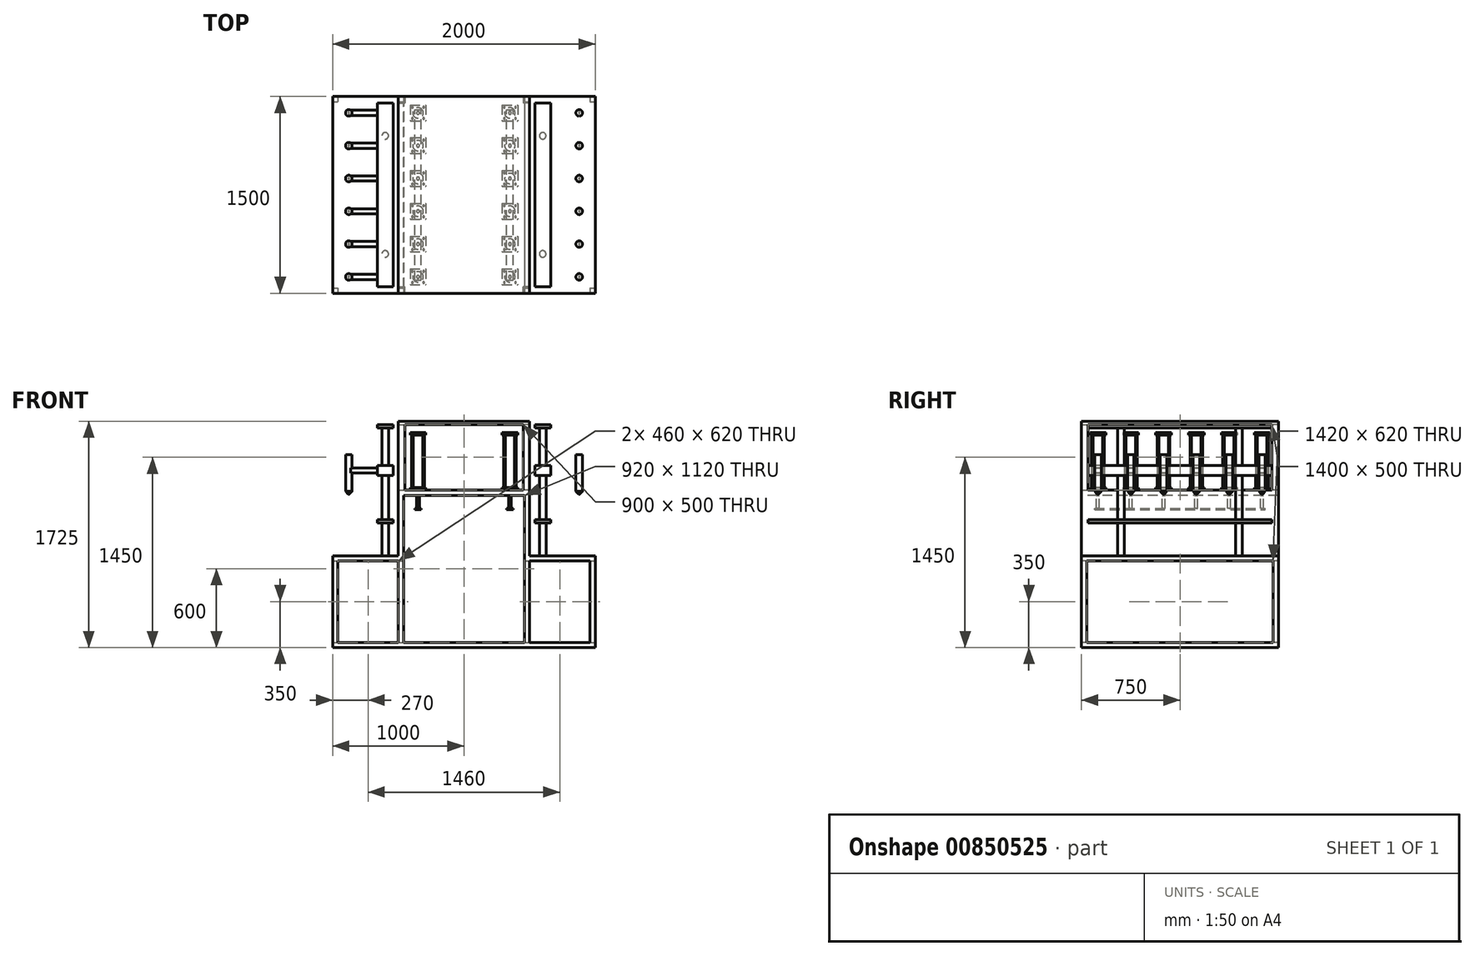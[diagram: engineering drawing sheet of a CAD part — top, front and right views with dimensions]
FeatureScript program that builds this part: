
annotation { "Feature Type Name" : "Feature", "Feature Type Description" : "" }
export const myFeature = defineFeature(function(context is Context, id is Id, definition is map)
    precondition{}
    {
        {
            var Q0;
            Q0=qCreatedBy(makeId("Front.planeOp"),FACE);
            var sketch = newSketch(context, id + "F0", { "sketchPlane" : qUnion([Q0])});
            skLineSegment(sketch, "E0", {"start": v(0, 0) * mm, "end": v(1000, 0) * mm});
            skLineSegment(sketch, "E1", {"start": v(1000, 0) * mm, "end": v(1000, 700) * mm});
            skLineSegment(sketch, "E2", {"start": v(1000, 700) * mm, "end": v(500, 700) * mm});
            skLineSegment(sketch, "E3", {"start": v(500, 700) * mm, "end": v(500, 1200) * mm});
            skLineSegment(sketch, "E4", {"start": v(500, 1200) * mm, "end": v(0, 1200) * mm});
            skLineSegment(sketch, "E5", {"start": v(0, 1200) * mm, "end": v(0, 0) * mm});
            skLineSegment(sketch, "E6.MirrorCS", {"start": v(-500, 1200) * mm, "end": v(0, 1200) * mm});
            skLineSegment(sketch, "E7.MirrorCS", {"start": v(-500, 700) * mm, "end": v(-500, 1200) * mm});
            skLineSegment(sketch, "E8.MirrorCS", {"start": v(-1000, 700) * mm, "end": v(-500, 700) * mm});
            skLineSegment(sketch, "E9.MirrorCS", {"start": v(-1000, 0) * mm, "end": v(-1000, 700) * mm});
            skLineSegment(sketch, "E10.MirrorCS", {"start": v(0, 0) * mm, "end": v(-1000, 0) * mm});
            skSolve(sketch);
        }
        {
            var Q0;
            Q0=makeQuery(id+"F0.imprint","IMPRINT",FACE,{"disambiguationData":[TD([[makeQuery(id+"F0.imprint","IMPRINT",EDGE,{"derivedFrom":sQuery(id+"F0.wireOp",EDGE,"E5")}),-1.0]])]});
            var Q1;
            Q1=makeQuery(id+"F0.imprint","IMPRINT",FACE,{"disambiguationData":[TD([[makeQuery(id+"F0.imprint","IMPRINT",EDGE,{"derivedFrom":sQuery(id+"F0.wireOp",EDGE,"E0")}),1.0]])]});
            extrude(context, id + "F1", {"entities" : qUnion([Q0, Q1]), "depth" : 1500 * mm, "offsetDistance" : 25 * mm});
        }
        {
            var Q0;
            Q0=makeQuery(id+"F1.opExtrude","CAP_FACE",FACE,{"disambiguationData":[OSD([sQuery(id+"F0.wireOp",EDGE,"E0"),sQuery(id+"F0.wireOp",EDGE,"E1"),sQuery(id+"F0.wireOp",EDGE,"E2"),sQuery(id+"F0.wireOp",EDGE,"E3"),sQuery(id+"F0.wireOp",EDGE,"E4"),sQuery(id+"F0.wireOp",EDGE,"E6.MirrorCS"),sQuery(id+"F0.wireOp",EDGE,"E7.MirrorCS"),sQuery(id+"F0.wireOp",EDGE,"E8.MirrorCS"),sQuery(id+"F0.wireOp",EDGE,"E9.MirrorCS"),sQuery(id+"F0.wireOp",EDGE,"E10.MirrorCS")])],"isStart":false});
            var sketch = newSketch(context, id + "F2", { "sketchPlane" : qUnion([Q0])});
            skLineSegment(sketch, "E11.0", {"start": v(-960, 660) * mm, "end": v(-960, 40) * mm});
            skLineSegment(sketch, "E11.1", {"start": v(-500, 660) * mm, "end": v(-960, 660) * mm});
            skLineSegment(sketch, "E11.2", {"start": v(-960, 40) * mm, "end": v(-500, 40) * mm});
            skLineSegment(sketch, "E11.3", {"start": v(-460, 1160) * mm, "end": v(-460, 660) * mm});
            skLineSegment(sketch, "E11.4", {"start": v(960, 40) * mm, "end": v(960, 660) * mm});
            skLineSegment(sketch, "E11.5", {"start": v(960, 660) * mm, "end": v(500, 660) * mm});
            skLineSegment(sketch, "E11.6", {"start": v(460, 660) * mm, "end": v(460, 1160) * mm});
            skLineSegment(sketch, "E11.7", {"start": v(460, 1160) * mm, "end": v(-460, 1160) * mm});
            skLineSegment(sketch, "E12", {"start": v(-460, 660) * mm, "end": v(-460, 40) * mm});
            skLineSegment(sketch, "E13.0", {"start": v(-500, 660) * mm, "end": v(-500, 40) * mm});
            skLineSegment(sketch, "E14.trimOffspring", {"start": v(-460, 40) * mm, "end": v(460, 40) * mm});
            skLineSegment(sketch, "E15", {"start": v(460, 660) * mm, "end": v(460, 40) * mm});
            skLineSegment(sketch, "E16.0", {"start": v(500, 660) * mm, "end": v(500, 40) * mm});
            skLineSegment(sketch, "E17.trimOffspring", {"start": v(500, 40) * mm, "end": v(960, 40) * mm});
            skSolve(sketch);
        }
        {
            var Q0;
            Q0=makeQuery(id+"F2.imprint","IMPRINT",FACE,{"disambiguationData":[TD([[makeQuery(id+"F2.imprint","IMPRINT",EDGE,{"derivedFrom":sQuery(id+"F2.wireOp",EDGE,"E11.0")}),1.0]])]});
            var Q1;
            Q1=makeQuery(id+"F2.imprint","IMPRINT",FACE,{"disambiguationData":[TD([[makeQuery(id+"F2.imprint","IMPRINT",EDGE,{"derivedFrom":sQuery(id+"F2.wireOp",EDGE,"E11.4")}),1.0]])]});
            var Q2;
            Q2=makeQuery(id+"F2.imprint","IMPRINT",FACE,{"disambiguationData":[TD([[makeQuery(id+"F2.imprint","IMPRINT",EDGE,{"derivedFrom":sQuery(id+"F2.wireOp",EDGE,"E11.3")}),1.0]])]});
            extrude(context, id + "F3", {"entities" : qUnion([Q0, Q1, Q2]), "operationType" : NewBodyOperationType.REMOVE, "endBound" : BoundingType.THROUGH_ALL, "oppositeDirection" : true, "depth" : 25 * mm, "offsetDistance" : 25 * mm});
        }
        {
            var Q0;
            Q0=makeQuery(id+"F1.opExtrude","SWEPT_FACE",FACE,{"disambiguationData":[OSD([sQuery(id+"F0.wireOp",EDGE,"E1")])]});
            var sketch = newSketch(context, id + "F4", { "sketchPlane" : qUnion([Q0])});
            skLineSegment(sketch, "E18.0", {"start": v(-40, 40) * mm, "end": v(-40, 660) * mm});
            skLineSegment(sketch, "E18.1", {"start": v(-1460, 40) * mm, "end": v(-40, 40) * mm});
            skLineSegment(sketch, "E18.2", {"start": v(-1460, 660) * mm, "end": v(-1460, 40) * mm});
            skLineSegment(sketch, "E18.3", {"start": v(-40, 660) * mm, "end": v(-1460, 660) * mm});
            skSolve(sketch);
        }
        {
            var Q0;
            Q0=makeQuery(id+"F4.imprint","IMPRINT",FACE,{"disambiguationData":[TD([[makeQuery(id+"F4.imprint","IMPRINT",EDGE,{"derivedFrom":sQuery(id+"F4.wireOp",EDGE,"E18.0")}),1.0]])]});
            extrude(context, id + "F5", {"entities" : qUnion([Q0]), "operationType" : NewBodyOperationType.REMOVE, "endBound" : BoundingType.THROUGH_ALL, "oppositeDirection" : true, "depth" : 25 * mm, "offsetDistance" : 25 * mm});
        }
        {
            var Q0;
            Q0=makeQuery(id+"F1.opExtrude","SWEPT_FACE",FACE,{"disambiguationData":[OSD([sQuery(id+"F0.wireOp",EDGE,"E4"),sQuery(id+"F0.wireOp",EDGE,"E6.MirrorCS")])]});
            var sketch = newSketch(context, id + "F6", { "sketchPlane" : qUnion([Q0])});
            skLineSegment(sketch, "E19.bottom", {"start": v(-410, -65) * mm, "end": v(-290, -65) * mm});
            skLineSegment(sketch, "E19.top", {"start": v(-410, -185) * mm, "end": v(-290, -185) * mm});
            skLineSegment(sketch, "E19.left", {"start": v(-410, -65) * mm, "end": v(-410, -185) * mm});
            skLineSegment(sketch, "E19.right", {"start": v(-290, -65) * mm, "end": v(-290, -185) * mm});
            skLineSegment(sketch, "E20.0.1.0", {"start": v(-410, -315) * mm, "end": v(-410, -435) * mm});
            skLineSegment(sketch, "E20.0.1.1", {"start": v(-290, -315) * mm, "end": v(-290, -435) * mm});
            skLineSegment(sketch, "E20.0.1.2", {"start": v(-410, -435) * mm, "end": v(-290, -435) * mm});
            skLineSegment(sketch, "E20.0.1.3", {"start": v(-410, -315) * mm, "end": v(-290, -315) * mm});
            skLineSegment(sketch, "E20.0.2.0", {"start": v(-410, -565) * mm, "end": v(-410, -685) * mm});
            skLineSegment(sketch, "E20.0.2.1", {"start": v(-290, -565) * mm, "end": v(-290, -685) * mm});
            skLineSegment(sketch, "E20.0.2.2", {"start": v(-410, -685) * mm, "end": v(-290, -685) * mm});
            skLineSegment(sketch, "E20.0.2.3", {"start": v(-410, -565) * mm, "end": v(-290, -565) * mm});
            skLineSegment(sketch, "E20.0.3.0", {"start": v(-410, -815) * mm, "end": v(-410, -935) * mm});
            skLineSegment(sketch, "E20.0.3.1", {"start": v(-290, -815) * mm, "end": v(-290, -935) * mm});
            skLineSegment(sketch, "E20.0.3.2", {"start": v(-410, -935) * mm, "end": v(-290, -935) * mm});
            skLineSegment(sketch, "E20.0.3.3", {"start": v(-410, -815) * mm, "end": v(-290, -815) * mm});
            skLineSegment(sketch, "E20.0.4.0", {"start": v(-410, -1065) * mm, "end": v(-410, -1185) * mm});
            skLineSegment(sketch, "E20.0.4.1", {"start": v(-290, -1065) * mm, "end": v(-290, -1185) * mm});
            skLineSegment(sketch, "E20.0.4.2", {"start": v(-410, -1185) * mm, "end": v(-290, -1185) * mm});
            skLineSegment(sketch, "E20.0.4.3", {"start": v(-410, -1065) * mm, "end": v(-290, -1065) * mm});
            skLineSegment(sketch, "E20.0.5.0", {"start": v(-410, -1315) * mm, "end": v(-410, -1435) * mm});
            skLineSegment(sketch, "E20.0.5.1", {"start": v(-290, -1315) * mm, "end": v(-290, -1435) * mm});
            skLineSegment(sketch, "E20.0.5.2", {"start": v(-410, -1435) * mm, "end": v(-290, -1435) * mm});
            skLineSegment(sketch, "E20.0.5.3", {"start": v(-410, -1315) * mm, "end": v(-290, -1315) * mm});
            skLineSegment(sketch, "E20.1.0.0", {"start": v(290, -65) * mm, "end": v(290, -185) * mm});
            skLineSegment(sketch, "E20.1.0.1", {"start": v(410, -65) * mm, "end": v(410, -185) * mm});
            skLineSegment(sketch, "E20.1.0.2", {"start": v(290, -185) * mm, "end": v(410, -185) * mm});
            skLineSegment(sketch, "E20.1.0.3", {"start": v(290, -65) * mm, "end": v(410, -65) * mm});
            skLineSegment(sketch, "E20.1.1.0", {"start": v(290, -315) * mm, "end": v(290, -435) * mm});
            skLineSegment(sketch, "E20.1.1.1", {"start": v(410, -315) * mm, "end": v(410, -435) * mm});
            skLineSegment(sketch, "E20.1.1.2", {"start": v(290, -435) * mm, "end": v(410, -435) * mm});
            skLineSegment(sketch, "E20.1.1.3", {"start": v(290, -315) * mm, "end": v(410, -315) * mm});
            skLineSegment(sketch, "E20.1.2.0", {"start": v(290, -565) * mm, "end": v(290, -685) * mm});
            skLineSegment(sketch, "E20.1.2.1", {"start": v(410, -565) * mm, "end": v(410, -685) * mm});
            skLineSegment(sketch, "E20.1.2.2", {"start": v(290, -685) * mm, "end": v(410, -685) * mm});
            skLineSegment(sketch, "E20.1.2.3", {"start": v(290, -565) * mm, "end": v(410, -565) * mm});
            skLineSegment(sketch, "E20.1.3.0", {"start": v(290, -815) * mm, "end": v(290, -935) * mm});
            skLineSegment(sketch, "E20.1.3.1", {"start": v(410, -815) * mm, "end": v(410, -935) * mm});
            skLineSegment(sketch, "E20.1.3.2", {"start": v(290, -935) * mm, "end": v(410, -935) * mm});
            skLineSegment(sketch, "E20.1.3.3", {"start": v(290, -815) * mm, "end": v(410, -815) * mm});
            skLineSegment(sketch, "E20.1.4.0", {"start": v(290, -1065) * mm, "end": v(290, -1185) * mm});
            skLineSegment(sketch, "E20.1.4.1", {"start": v(410, -1065) * mm, "end": v(410, -1185) * mm});
            skLineSegment(sketch, "E20.1.4.2", {"start": v(290, -1185) * mm, "end": v(410, -1185) * mm});
            skLineSegment(sketch, "E20.1.4.3", {"start": v(290, -1065) * mm, "end": v(410, -1065) * mm});
            skLineSegment(sketch, "E20.1.5.0", {"start": v(290, -1315) * mm, "end": v(290, -1435) * mm});
            skLineSegment(sketch, "E20.1.5.1", {"start": v(410, -1315) * mm, "end": v(410, -1435) * mm});
            skLineSegment(sketch, "E20.1.5.2", {"start": v(290, -1435) * mm, "end": v(410, -1435) * mm});
            skLineSegment(sketch, "E20.1.5.3", {"start": v(290, -1315) * mm, "end": v(410, -1315) * mm});
            skLineSegment(sketch, "E20.direction1", {"start": v(-410, -185) * mm, "end": v(290, -185) * mm, "construction": true});
            skLineSegment(sketch, "E20.direction2", {"start": v(-410, -185) * mm, "end": v(-410, -435) * mm, "construction": true});
            skSolve(sketch);
        }
        {
            var Q0;
            Q0 = qSketchRegion(id + "F6", true);
            extrude(context, id + "F7", {"entities" : qUnion([Q0]), "operationType" : NewBodyOperationType.ADD, "depth" : 20 * mm, "offsetDistance" : 25 * mm});
        }
        {
            var Q0;
            Q0=makeQuery(id+"F7.opExtrude","CAP_FACE",FACE,{"disambiguationData":[OSD([sQuery(id+"F6.wireOp",EDGE,"E20.0.5.0"),sQuery(id+"F6.wireOp",EDGE,"E20.0.5.1"),sQuery(id+"F6.wireOp",EDGE,"E20.0.5.2"),sQuery(id+"F6.wireOp",EDGE,"E20.0.5.3")])],"isStart":false});
            var sketch = newSketch(context, id + "F8", { "sketchPlane" : qUnion([Q0])});
            skCircle(sketch, "E21", {"center": v(-350, -1375) * mm, "radius": 40 * mm});
            skPoint(sketch, "E21.centerSnap0", {"position": v(-290, -1375) * mm});
            skPoint(sketch, "E21.centerSnap1", {"position": v(-350, -1315) * mm});
            skCircle(sketch, "E22.0.1.0", {"center": v(-350, -1125) * mm, "radius": 40 * mm});
            skCircle(sketch, "E22.0.2.0", {"center": v(-350, -875) * mm, "radius": 40 * mm});
            skCircle(sketch, "E22.0.3.0", {"center": v(-350, -625) * mm, "radius": 40 * mm});
            skCircle(sketch, "E22.0.4.0", {"center": v(-350, -375) * mm, "radius": 40 * mm});
            skCircle(sketch, "E22.0.5.0", {"center": v(-350, -125) * mm, "radius": 40 * mm});
            skCircle(sketch, "E22.1.0.0", {"center": v(350, -1375) * mm, "radius": 40 * mm});
            skCircle(sketch, "E22.1.1.0", {"center": v(350, -1125) * mm, "radius": 40 * mm});
            skCircle(sketch, "E22.1.2.0", {"center": v(350, -875) * mm, "radius": 40 * mm});
            skCircle(sketch, "E22.1.3.0", {"center": v(350, -625) * mm, "radius": 40 * mm});
            skCircle(sketch, "E22.1.4.0", {"center": v(350, -375) * mm, "radius": 40 * mm});
            skCircle(sketch, "E22.1.5.0", {"center": v(350, -125) * mm, "radius": 40 * mm});
            skLineSegment(sketch, "E22.direction1", {"start": v(-350, -1375) * mm, "end": v(350, -1375) * mm, "construction": true});
            skLineSegment(sketch, "E22.direction2", {"start": v(-350, -1375) * mm, "end": v(-350, -1125) * mm, "construction": true});
            skSolve(sketch);
        }
        {
            var Q0;
            Q0 = qSketchRegion(id + "F8", true);
            extrude(context, id + "F9", {"entities" : qUnion([Q0]), "operationType" : NewBodyOperationType.ADD, "depth" : 400 * mm, "offsetDistance" : 25 * mm});
        }
        {
            var Q0;
            Q0=makeQuery(id+"F7.opExtrude","CAP_FACE",FACE,{"disambiguationData":[OSD([sQuery(id+"F6.wireOp",EDGE,"E20.0.5.0"),sQuery(id+"F6.wireOp",EDGE,"E20.0.5.1"),sQuery(id+"F6.wireOp",EDGE,"E20.0.5.2"),sQuery(id+"F6.wireOp",EDGE,"E20.0.5.3")])],"isStart":false});
            var sketch = newSketch(context, id + "F10", { "sketchPlane" : qUnion([Q0])});
            skCircle(sketch, "E23", {"center": v(-307.5, -1332.5) * mm, "radius": 6 * mm});
            skCircle(sketch, "E24", {"center": v(-392.5, -1332.5) * mm, "radius": 6 * mm});
            skCircle(sketch, "E25", {"center": v(-307.5, -1417.5) * mm, "radius": 6 * mm});
            skCircle(sketch, "E26", {"center": v(-392.5, -1417.5) * mm, "radius": 6 * mm});
            skCircle(sketch, "E27.0.1.0", {"center": v(-307.5, -1082.5) * mm, "radius": 6 * mm});
            skCircle(sketch, "E27.0.1.1", {"center": v(-392.5, -1082.5) * mm, "radius": 6 * mm});
            skCircle(sketch, "E27.0.1.2", {"center": v(-392.5, -1167.5) * mm, "radius": 6 * mm});
            skCircle(sketch, "E27.0.1.3", {"center": v(-307.5, -1167.5) * mm, "radius": 6 * mm});
            skCircle(sketch, "E27.0.2.0", {"center": v(-307.5, -832.5) * mm, "radius": 6 * mm});
            skCircle(sketch, "E27.0.2.1", {"center": v(-392.5, -832.5) * mm, "radius": 6 * mm});
            skCircle(sketch, "E27.0.2.2", {"center": v(-392.5, -917.5) * mm, "radius": 6 * mm});
            skCircle(sketch, "E27.0.2.3", {"center": v(-307.5, -917.5) * mm, "radius": 6 * mm});
            skCircle(sketch, "E27.0.3.0", {"center": v(-307.5, -582.5) * mm, "radius": 6 * mm});
            skCircle(sketch, "E27.0.3.1", {"center": v(-392.5, -582.5) * mm, "radius": 6 * mm});
            skCircle(sketch, "E27.0.3.2", {"center": v(-392.5, -667.5) * mm, "radius": 6 * mm});
            skCircle(sketch, "E27.0.3.3", {"center": v(-307.5, -667.5) * mm, "radius": 6 * mm});
            skCircle(sketch, "E27.0.4.0", {"center": v(-307.5, -332.5) * mm, "radius": 6 * mm});
            skCircle(sketch, "E27.0.4.1", {"center": v(-392.5, -332.5) * mm, "radius": 6 * mm});
            skCircle(sketch, "E27.0.4.2", {"center": v(-392.5, -417.5) * mm, "radius": 6 * mm});
            skCircle(sketch, "E27.0.4.3", {"center": v(-307.5, -417.5) * mm, "radius": 6 * mm});
            skCircle(sketch, "E27.0.5.0", {"center": v(-307.5, -82.5) * mm, "radius": 6 * mm});
            skCircle(sketch, "E27.0.5.1", {"center": v(-392.5, -82.5) * mm, "radius": 6 * mm});
            skCircle(sketch, "E27.0.5.2", {"center": v(-392.5, -167.5) * mm, "radius": 6 * mm});
            skCircle(sketch, "E27.0.5.3", {"center": v(-307.5, -167.5) * mm, "radius": 6 * mm});
            skCircle(sketch, "E27.1.0.0", {"center": v(392.5, -1332.5) * mm, "radius": 6 * mm});
            skCircle(sketch, "E27.1.0.1", {"center": v(307.5, -1332.5) * mm, "radius": 6 * mm});
            skCircle(sketch, "E27.1.0.2", {"center": v(307.5, -1417.5) * mm, "radius": 6 * mm});
            skCircle(sketch, "E27.1.0.3", {"center": v(392.5, -1417.5) * mm, "radius": 6 * mm});
            skCircle(sketch, "E27.1.1.0", {"center": v(392.5, -1082.5) * mm, "radius": 6 * mm});
            skCircle(sketch, "E27.1.1.1", {"center": v(307.5, -1082.5) * mm, "radius": 6 * mm});
            skCircle(sketch, "E27.1.1.2", {"center": v(307.5, -1167.5) * mm, "radius": 6 * mm});
            skCircle(sketch, "E27.1.1.3", {"center": v(392.5, -1167.5) * mm, "radius": 6 * mm});
            skCircle(sketch, "E27.1.2.0", {"center": v(392.5, -832.5) * mm, "radius": 6 * mm});
            skCircle(sketch, "E27.1.2.1", {"center": v(307.5, -832.5) * mm, "radius": 6 * mm});
            skCircle(sketch, "E27.1.2.2", {"center": v(307.5, -917.5) * mm, "radius": 6 * mm});
            skCircle(sketch, "E27.1.2.3", {"center": v(392.5, -917.5) * mm, "radius": 6 * mm});
            skCircle(sketch, "E27.1.3.0", {"center": v(392.5, -582.5) * mm, "radius": 6 * mm});
            skCircle(sketch, "E27.1.3.1", {"center": v(307.5, -582.5) * mm, "radius": 6 * mm});
            skCircle(sketch, "E27.1.3.2", {"center": v(307.5, -667.5) * mm, "radius": 6 * mm});
            skCircle(sketch, "E27.1.3.3", {"center": v(392.5, -667.5) * mm, "radius": 6 * mm});
            skCircle(sketch, "E27.1.4.0", {"center": v(392.5, -332.5) * mm, "radius": 6 * mm});
            skCircle(sketch, "E27.1.4.1", {"center": v(307.5, -332.5) * mm, "radius": 6 * mm});
            skCircle(sketch, "E27.1.4.2", {"center": v(307.5, -417.5) * mm, "radius": 6 * mm});
            skCircle(sketch, "E27.1.4.3", {"center": v(392.5, -417.5) * mm, "radius": 6 * mm});
            skCircle(sketch, "E27.1.5.0", {"center": v(392.5, -82.5) * mm, "radius": 6 * mm});
            skCircle(sketch, "E27.1.5.1", {"center": v(307.5, -82.5) * mm, "radius": 6 * mm});
            skCircle(sketch, "E27.1.5.2", {"center": v(307.5, -167.5) * mm, "radius": 6 * mm});
            skCircle(sketch, "E27.1.5.3", {"center": v(392.5, -167.5) * mm, "radius": 6 * mm});
            skLineSegment(sketch, "E27.direction1", {"start": v(-392.5, -1417.5) * mm, "end": v(307.5, -1417.5) * mm, "construction": true});
            skLineSegment(sketch, "E27.direction2", {"start": v(-392.5, -1417.5) * mm, "end": v(-392.5, -1167.5) * mm, "construction": true});
            skSolve(sketch);
        }
        {
            var Q0;
            Q0 = qSketchRegion(id + "F10", true);
            extrude(context, id + "F11", {"entities" : qUnion([Q0]), "operationType" : NewBodyOperationType.ADD, "depth" : 400 * mm, "offsetDistance" : 25 * mm});
        }
        {
            var Q0;
            Q0=makeQuery(id+"F9.opExtrude","CAP_FACE",FACE,{"disambiguationData":[OSD([sQuery(id+"F8.wireOp",EDGE,"E21")])],"isStart":false});
            var sketch = newSketch(context, id + "F12", { "sketchPlane" : qUnion([Q0])});
            skLineSegment(sketch, "E28.bottom", {"start": v(-410, -1315) * mm, "end": v(-290, -1315) * mm});
            skLineSegment(sketch, "E28.top", {"start": v(-410, -1435) * mm, "end": v(-290, -1435) * mm});
            skLineSegment(sketch, "E28.left", {"start": v(-410, -1315) * mm, "end": v(-410, -1435) * mm});
            skLineSegment(sketch, "E28.right", {"start": v(-290, -1315) * mm, "end": v(-290, -1435) * mm});
            skLineSegment(sketch, "E29.0.1.0", {"start": v(-410, -1065) * mm, "end": v(-410, -1185) * mm});
            skLineSegment(sketch, "E29.0.1.1", {"start": v(-410, -1185) * mm, "end": v(-290, -1185) * mm});
            skLineSegment(sketch, "E29.0.1.2", {"start": v(-290, -1065) * mm, "end": v(-290, -1185) * mm});
            skLineSegment(sketch, "E29.0.1.3", {"start": v(-410, -1065) * mm, "end": v(-290, -1065) * mm});
            skLineSegment(sketch, "E29.0.2.0", {"start": v(-410, -815) * mm, "end": v(-410, -935) * mm});
            skLineSegment(sketch, "E29.0.2.1", {"start": v(-410, -935) * mm, "end": v(-290, -935) * mm});
            skLineSegment(sketch, "E29.0.2.2", {"start": v(-290, -815) * mm, "end": v(-290, -935) * mm});
            skLineSegment(sketch, "E29.0.2.3", {"start": v(-410, -815) * mm, "end": v(-290, -815) * mm});
            skLineSegment(sketch, "E29.0.3.0", {"start": v(-410, -565) * mm, "end": v(-410, -685) * mm});
            skLineSegment(sketch, "E29.0.3.1", {"start": v(-410, -685) * mm, "end": v(-290, -685) * mm});
            skLineSegment(sketch, "E29.0.3.2", {"start": v(-290, -565) * mm, "end": v(-290, -685) * mm});
            skLineSegment(sketch, "E29.0.3.3", {"start": v(-410, -565) * mm, "end": v(-290, -565) * mm});
            skLineSegment(sketch, "E29.0.4.0", {"start": v(-410, -315) * mm, "end": v(-410, -435) * mm});
            skLineSegment(sketch, "E29.0.4.1", {"start": v(-410, -435) * mm, "end": v(-290, -435) * mm});
            skLineSegment(sketch, "E29.0.4.2", {"start": v(-290, -315) * mm, "end": v(-290, -435) * mm});
            skLineSegment(sketch, "E29.0.4.3", {"start": v(-410, -315) * mm, "end": v(-290, -315) * mm});
            skLineSegment(sketch, "E29.0.5.0", {"start": v(-410, -65) * mm, "end": v(-410, -185) * mm});
            skLineSegment(sketch, "E29.0.5.1", {"start": v(-410, -185) * mm, "end": v(-290, -185) * mm});
            skLineSegment(sketch, "E29.0.5.2", {"start": v(-290, -65) * mm, "end": v(-290, -185) * mm});
            skLineSegment(sketch, "E29.0.5.3", {"start": v(-410, -65) * mm, "end": v(-290, -65) * mm});
            skLineSegment(sketch, "E29.1.0.0", {"start": v(290, -1315) * mm, "end": v(290, -1435) * mm});
            skLineSegment(sketch, "E29.1.0.1", {"start": v(290, -1435) * mm, "end": v(410, -1435) * mm});
            skLineSegment(sketch, "E29.1.0.2", {"start": v(410, -1315) * mm, "end": v(410, -1435) * mm});
            skLineSegment(sketch, "E29.1.0.3", {"start": v(290, -1315) * mm, "end": v(410, -1315) * mm});
            skLineSegment(sketch, "E29.1.1.0", {"start": v(290, -1065) * mm, "end": v(290, -1185) * mm});
            skLineSegment(sketch, "E29.1.1.1", {"start": v(290, -1185) * mm, "end": v(410, -1185) * mm});
            skLineSegment(sketch, "E29.1.1.2", {"start": v(410, -1065) * mm, "end": v(410, -1185) * mm});
            skLineSegment(sketch, "E29.1.1.3", {"start": v(290, -1065) * mm, "end": v(410, -1065) * mm});
            skLineSegment(sketch, "E29.1.2.0", {"start": v(290, -815) * mm, "end": v(290, -935) * mm});
            skLineSegment(sketch, "E29.1.2.1", {"start": v(290, -935) * mm, "end": v(410, -935) * mm});
            skLineSegment(sketch, "E29.1.2.2", {"start": v(410, -815) * mm, "end": v(410, -935) * mm});
            skLineSegment(sketch, "E29.1.2.3", {"start": v(290, -815) * mm, "end": v(410, -815) * mm});
            skLineSegment(sketch, "E29.1.3.0", {"start": v(290, -565) * mm, "end": v(290, -685) * mm});
            skLineSegment(sketch, "E29.1.3.1", {"start": v(290, -685) * mm, "end": v(410, -685) * mm});
            skLineSegment(sketch, "E29.1.3.2", {"start": v(410, -565) * mm, "end": v(410, -685) * mm});
            skLineSegment(sketch, "E29.1.3.3", {"start": v(290, -565) * mm, "end": v(410, -565) * mm});
            skLineSegment(sketch, "E29.1.4.0", {"start": v(290, -315) * mm, "end": v(290, -435) * mm});
            skLineSegment(sketch, "E29.1.4.1", {"start": v(290, -435) * mm, "end": v(410, -435) * mm});
            skLineSegment(sketch, "E29.1.4.2", {"start": v(410, -315) * mm, "end": v(410, -435) * mm});
            skLineSegment(sketch, "E29.1.4.3", {"start": v(290, -315) * mm, "end": v(410, -315) * mm});
            skLineSegment(sketch, "E29.1.5.0", {"start": v(290, -65) * mm, "end": v(290, -185) * mm});
            skLineSegment(sketch, "E29.1.5.1", {"start": v(290, -185) * mm, "end": v(410, -185) * mm});
            skLineSegment(sketch, "E29.1.5.2", {"start": v(410, -65) * mm, "end": v(410, -185) * mm});
            skLineSegment(sketch, "E29.1.5.3", {"start": v(290, -65) * mm, "end": v(410, -65) * mm});
            skLineSegment(sketch, "E29.direction1", {"start": v(-410, -1435) * mm, "end": v(290, -1435) * mm, "construction": true});
            skLineSegment(sketch, "E29.direction2", {"start": v(-410, -1435) * mm, "end": v(-410, -1185) * mm, "construction": true});
            skSolve(sketch);
        }
        {
            var Q0;
            Q0 = qSketchRegion(id + "F12", true);
            extrude(context, id + "F13", {"entities" : qUnion([Q0]), "operationType" : NewBodyOperationType.ADD, "depth" : 20 * mm, "offsetDistance" : 25 * mm});
        }
        {
            var Q0;
            Q0=makeQuery(id+"F3.boolean.opBoolean","COPY",FACE,{"derivedFrom":makeQuery(id+"F3.opExtrude","SWEPT_FACE",FACE,{"disambiguationData":[OSD([sQuery(id+"F2.wireOp",EDGE,"E11.7")])]})});
            var sketch = newSketch(context, id + "F14", { "sketchPlane" : qUnion([Q0])});
            skCircle(sketch, "E30", {"center": v(-350, 125) * mm, "radius": 11 * mm});
            skCircle(sketch, "E31.0.1.0", {"center": v(-350, 375) * mm, "radius": 11 * mm});
            skCircle(sketch, "E31.0.2.0", {"center": v(-350, 625) * mm, "radius": 11 * mm});
            skCircle(sketch, "E31.0.3.0", {"center": v(-350, 875) * mm, "radius": 11 * mm});
            skCircle(sketch, "E31.0.4.0", {"center": v(-350, 1125) * mm, "radius": 11 * mm});
            skCircle(sketch, "E31.0.5.0", {"center": v(-350, 1375) * mm, "radius": 11 * mm});
            skCircle(sketch, "E31.1.0.0", {"center": v(350, 125) * mm, "radius": 11 * mm});
            skCircle(sketch, "E31.1.1.0", {"center": v(350, 375) * mm, "radius": 11 * mm});
            skCircle(sketch, "E31.1.2.0", {"center": v(350, 625) * mm, "radius": 11 * mm});
            skCircle(sketch, "E31.1.3.0", {"center": v(350, 875) * mm, "radius": 11 * mm});
            skCircle(sketch, "E31.1.4.0", {"center": v(350, 1125) * mm, "radius": 11 * mm});
            skCircle(sketch, "E31.1.5.0", {"center": v(350, 1375) * mm, "radius": 11 * mm});
            skLineSegment(sketch, "E31.direction1", {"start": v(-350, 125) * mm, "end": v(350, 125) * mm, "construction": true});
            skLineSegment(sketch, "E31.direction2", {"start": v(-350, 125) * mm, "end": v(-350, 375) * mm, "construction": true});
            skSolve(sketch);
        }
        {
            var Q0;
            Q0 = qSketchRegion(id + "F14", true);
            extrude(context, id + "F15", {"entities" : qUnion([Q0]), "operationType" : NewBodyOperationType.ADD, "depth" : 100 * mm, "offsetDistance" : 25 * mm});
        }
        {
            var Q0;
            Q0=makeQuery(id+"F15.opExtrude","CAP_FACE",FACE,{"disambiguationData":[OSD([sQuery(id+"F14.wireOp",EDGE,"E31.0.5.0")])],"isStart":false});
            var sketch = newSketch(context, id + "F16", { "sketchPlane" : qUnion([Q0])});
            skLineSegment(sketch, "E32.bottom", {"start": v(-375, 1400) * mm, "end": v(-325, 1400) * mm});
            skLineSegment(sketch, "E32.top", {"start": v(-375, 100) * mm, "end": v(-325, 100) * mm});
            skLineSegment(sketch, "E32.left", {"start": v(-375, 1400) * mm, "end": v(-375, 100) * mm});
            skLineSegment(sketch, "E32.right", {"start": v(-325, 1400) * mm, "end": v(-325, 100) * mm});
            skLineSegment(sketch, "E33.1.0.0", {"start": v(325, 1400) * mm, "end": v(375, 1400) * mm});
            skLineSegment(sketch, "E33.1.0.1", {"start": v(325, 100) * mm, "end": v(375, 100) * mm});
            skLineSegment(sketch, "E33.1.0.2", {"start": v(325, 1400) * mm, "end": v(325, 100) * mm});
            skLineSegment(sketch, "E33.1.0.3", {"start": v(375, 1400) * mm, "end": v(375, 100) * mm});
            skLineSegment(sketch, "E33.direction1", {"start": v(-375, 100) * mm, "end": v(325, 100) * mm, "construction": true});
            skSolve(sketch);
        }
        {
            var Q0;
            Q0 = qSketchRegion(id + "F16", true);
            extrude(context, id + "F17", {"entities" : qUnion([Q0]), "operationType" : NewBodyOperationType.ADD, "depth" : 10 * mm, "offsetDistance" : 25 * mm});
        }
        {
            var Q0;
            Q0=makeQuery(id+"F1.opExtrude","SWEPT_FACE",FACE,{"disambiguationData":[OSD([sQuery(id+"F0.wireOp",EDGE,"E8.MirrorCS")])]});
            var sketch = newSketch(context, id + "F18", { "sketchPlane" : qUnion([Q0])});
            skCircle(sketch, "E34", {"center": v(-600, -300) * mm, "radius": 25 * mm});
            skCircle(sketch, "E35.MirrorC", {"center": v(600, -300) * mm, "radius": 25 * mm});
            skCircle(sketch, "E36", {"center": v(-600, -1200) * mm, "radius": 25 * mm});
            skCircle(sketch, "E37.MirrorC", {"center": v(600, -1200) * mm, "radius": 25 * mm});
            skSolve(sketch);
        }
        {
            var Q0;
            Q0 = qSketchRegion(id + "F18", true);
            extrude(context, id + "F19", {"entities" : qUnion([Q0]), "operationType" : NewBodyOperationType.ADD, "depth" : 1000 * mm, "offsetDistance" : 25 * mm});
        }
        {
            var Q0;
            Q0=makeQuery(id+"F1.opExtrude","SWEPT_FACE",FACE,{"disambiguationData":[OSD([sQuery(id+"F0.wireOp",EDGE,"E8.MirrorCS")])]});
            cPlane(context, id + "F20", {"entities" : qUnion([Q0]), "cplaneType" : CPlaneType.OFFSET, "offset" : 250 * mm, "width" : 150 * mm, "height" : 150 * mm});
        }
        {
            var Q0;
            Q0=qCreatedBy(id+"F20.planeOp",FACE);
            var sketch = newSketch(context, id + "F21", { "sketchPlane" : qUnion([Q0])});
            skLineSegment(sketch, "E38.bottom", {"start": v(-660, -50) * mm, "end": v(-540, -50) * mm});
            skLineSegment(sketch, "E38.top", {"start": v(-660, -1450) * mm, "end": v(-540, -1450) * mm});
            skLineSegment(sketch, "E38.left", {"start": v(-660, -50) * mm, "end": v(-660, -1450) * mm});
            skLineSegment(sketch, "E38.right", {"start": v(-540, -50) * mm, "end": v(-540, -1450) * mm});
            skLineSegment(sketch, "E39.MirrorCS", {"start": v(540, -50) * mm, "end": v(540, -1450) * mm});
            skLineSegment(sketch, "E40.MirrorCS", {"start": v(660, -50) * mm, "end": v(660, -1450) * mm});
            skLineSegment(sketch, "E41.MirrorCS", {"start": v(660, -50) * mm, "end": v(540, -50) * mm});
            skLineSegment(sketch, "E42.MirrorCS", {"start": v(660, -1450) * mm, "end": v(540, -1450) * mm});
            skSolve(sketch);
        }
        {
            var Q0;
            Q0 = qSketchRegion(id + "F21", true);
            extrude(context, id + "F22", {"entities" : qUnion([Q0]), "operationType" : NewBodyOperationType.ADD, "depth" : 25 * mm, "offsetDistance" : 25 * mm});
        }
        {
            var Q0;
            Q0=makeQuery(id+"F19.opExtrude","CAP_FACE",FACE,{"disambiguationData":[OSD([sQuery(id+"F18.wireOp",EDGE,"E34")])],"isStart":false});
            var sketch = newSketch(context, id + "F23", { "sketchPlane" : qUnion([Q0])});
            skLineSegment(sketch, "E43.bottom", {"start": v(-660, -50) * mm, "end": v(-540, -50) * mm});
            skLineSegment(sketch, "E43.top", {"start": v(-660, -1450) * mm, "end": v(-540, -1450) * mm});
            skLineSegment(sketch, "E43.left", {"start": v(-660, -50) * mm, "end": v(-660, -1450) * mm});
            skLineSegment(sketch, "E43.right", {"start": v(-540, -50) * mm, "end": v(-540, -1450) * mm});
            skLineSegment(sketch, "E44.MirrorCS", {"start": v(660, -50) * mm, "end": v(540, -50) * mm});
            skLineSegment(sketch, "E45.MirrorCS", {"start": v(660, -50) * mm, "end": v(660, -1450) * mm});
            skLineSegment(sketch, "E46.MirrorCS", {"start": v(540, -50) * mm, "end": v(540, -1450) * mm});
            skLineSegment(sketch, "E47.MirrorCS", {"start": v(660, -1450) * mm, "end": v(540, -1450) * mm});
            skSolve(sketch);
        }
        {
            var Q0;
            Q0 = qSketchRegion(id + "F23", true);
            extrude(context, id + "F24", {"entities" : qUnion([Q0]), "operationType" : NewBodyOperationType.ADD, "oppositeDirection" : true, "depth" : 25 * mm, "offsetDistance" : 25 * mm});
        }
        {
            var Q0;
            Q0=makeQuery(id+"F22.opExtrude","CAP_FACE",FACE,{"disambiguationData":[OSD([sQuery(id+"F21.wireOp",EDGE,"E38.bottom"),sQuery(id+"F21.wireOp",EDGE,"E38.top"),sQuery(id+"F21.wireOp",EDGE,"E38.left"),sQuery(id+"F21.wireOp",EDGE,"E38.right")])],"isStart":false});
            cPlane(context, id + "F25", {"entities" : qUnion([Q0]), "cplaneType" : CPlaneType.OFFSET, "offset" : (675 / 2) * mm, "width" : 150 * mm, "height" : 150 * mm});
        }
        {
            var Q0;
            Q0=qCreatedBy(id+"F25.planeOp",FACE);
            var sketch = newSketch(context, id + "F26", { "sketchPlane" : qUnion([Q0])});
            skLineSegment(sketch, "E48.bottom", {"start": v(-660, -50) * mm, "end": v(-540, -50) * mm});
            skLineSegment(sketch, "E48.top", {"start": v(-660, -1450) * mm, "end": v(-540, -1450) * mm});
            skLineSegment(sketch, "E48.left", {"start": v(-660, -50) * mm, "end": v(-660, -1450) * mm});
            skLineSegment(sketch, "E48.right", {"start": v(-540, -50) * mm, "end": v(-540, -1450) * mm});
            skLineSegment(sketch, "E49.MirrorCS", {"start": v(660, -50) * mm, "end": v(540, -50) * mm});
            skLineSegment(sketch, "E50.MirrorCS", {"start": v(660, -50) * mm, "end": v(660, -1450) * mm});
            skLineSegment(sketch, "E51.MirrorCS", {"start": v(540, -50) * mm, "end": v(540, -1450) * mm});
            skLineSegment(sketch, "E52.MirrorCS", {"start": v(660, -1450) * mm, "end": v(540, -1450) * mm});
            skSolve(sketch);
        }
        {
            var Q0;
            Q0 = qSketchRegion(id + "F26", true);
            extrude(context, id + "F27", {"entities" : qUnion([Q0]), "operationType" : NewBodyOperationType.ADD, "depth" : 75 * mm, "offsetDistance" : 25 * mm});
        }
        {
            var Q0;
            Q0=makeQuery(id+"F27.opExtrude","SWEPT_FACE",FACE,{"disambiguationData":[OSD([sQuery(id+"F26.wireOp",EDGE,"E48.left")])]});
            var sketch = newSketch(context, id + "F28", { "sketchPlane" : qUnion([Q0])});
            skLineSegment(sketch, "E53.bottom", {"start": v(105, 1370) * mm, "end": v(145, 1370) * mm});
            skLineSegment(sketch, "E53.top", {"start": v(105, 1330) * mm, "end": v(145, 1330) * mm});
            skLineSegment(sketch, "E53.left", {"start": v(105, 1370) * mm, "end": v(105, 1330) * mm});
            skLineSegment(sketch, "E53.right", {"start": v(145, 1370) * mm, "end": v(145, 1330) * mm});
            skLineSegment(sketch, "E54.1.0.0", {"start": v(395, 1370) * mm, "end": v(395, 1330) * mm});
            skLineSegment(sketch, "E54.1.0.1", {"start": v(355, 1330) * mm, "end": v(395, 1330) * mm});
            skLineSegment(sketch, "E54.1.0.2", {"start": v(355, 1370) * mm, "end": v(395, 1370) * mm});
            skLineSegment(sketch, "E54.1.0.3", {"start": v(355, 1370) * mm, "end": v(355, 1330) * mm});
            skLineSegment(sketch, "E54.2.0.0", {"start": v(645, 1370) * mm, "end": v(645, 1330) * mm});
            skLineSegment(sketch, "E54.2.0.1", {"start": v(605, 1330) * mm, "end": v(645, 1330) * mm});
            skLineSegment(sketch, "E54.2.0.2", {"start": v(605, 1370) * mm, "end": v(645, 1370) * mm});
            skLineSegment(sketch, "E54.2.0.3", {"start": v(605, 1370) * mm, "end": v(605, 1330) * mm});
            skLineSegment(sketch, "E54.3.0.0", {"start": v(895, 1370) * mm, "end": v(895, 1330) * mm});
            skLineSegment(sketch, "E54.3.0.1", {"start": v(855, 1330) * mm, "end": v(895, 1330) * mm});
            skLineSegment(sketch, "E54.3.0.2", {"start": v(855, 1370) * mm, "end": v(895, 1370) * mm});
            skLineSegment(sketch, "E54.3.0.3", {"start": v(855, 1370) * mm, "end": v(855, 1330) * mm});
            skLineSegment(sketch, "E54.4.0.0", {"start": v(1145, 1370) * mm, "end": v(1145, 1330) * mm});
            skLineSegment(sketch, "E54.4.0.1", {"start": v(1105, 1330) * mm, "end": v(1145, 1330) * mm});
            skLineSegment(sketch, "E54.4.0.2", {"start": v(1105, 1370) * mm, "end": v(1145, 1370) * mm});
            skLineSegment(sketch, "E54.4.0.3", {"start": v(1105, 1370) * mm, "end": v(1105, 1330) * mm});
            skLineSegment(sketch, "E54.5.0.0", {"start": v(1395, 1370) * mm, "end": v(1395, 1330) * mm});
            skLineSegment(sketch, "E54.5.0.1", {"start": v(1355, 1330) * mm, "end": v(1395, 1330) * mm});
            skLineSegment(sketch, "E54.5.0.2", {"start": v(1355, 1370) * mm, "end": v(1395, 1370) * mm});
            skLineSegment(sketch, "E54.5.0.3", {"start": v(1355, 1370) * mm, "end": v(1355, 1330) * mm});
            skLineSegment(sketch, "E54.direction1", {"start": v(105, 1330) * mm, "end": v(355, 1330) * mm, "construction": true});
            skSolve(sketch);
        }
        {
            var Q0;
            Q0 = qSketchRegion(id + "F28", true);
            extrude(context, id + "F29", {"entities" : qUnion([Q0]), "operationType" : NewBodyOperationType.ADD, "depth" : 217.5 * mm, "offsetDistance" : 25 * mm});
        }
        {
            var Q0;
            Q0=makeQuery(id+"F29.opExtrude","SWEPT_FACE",FACE,{"disambiguationData":[OSD([sQuery(id+"F28.wireOp",EDGE,"E53.bottom")])]});
            var sketch = newSketch(context, id + "F30", { "sketchPlane" : qUnion([Q0])});
            skCircle(sketch, "E55", {"center": v(-877.5, -125) * mm, "radius": 25 * mm});
            skCircle(sketch, "E56.0.1.0", {"center": v(-877.5, -375) * mm, "radius": 25 * mm});
            skCircle(sketch, "E56.0.2.0", {"center": v(-877.5, -625) * mm, "radius": 25 * mm});
            skCircle(sketch, "E56.0.3.0", {"center": v(-877.5, -875) * mm, "radius": 25 * mm});
            skCircle(sketch, "E56.0.4.0", {"center": v(-877.5, -1125) * mm, "radius": 25 * mm});
            skCircle(sketch, "E56.0.5.0", {"center": v(-877.5, -1375) * mm, "radius": 25 * mm});
            skLineSegment(sketch, "E56.direction1", {"start": v(-877.5, -125) * mm, "end": v(-852.5, -125) * mm, "construction": true});
            skLineSegment(sketch, "E56.direction2", {"start": v(-877.5, -125) * mm, "end": v(-877.5, -375) * mm, "construction": true});
            skCircle(sketch, "E57.MirrorC", {"center": v(877.5, -125) * mm, "radius": 25 * mm});
            skCircle(sketch, "E58.MirrorC", {"center": v(877.5, -375) * mm, "radius": 25 * mm});
            skCircle(sketch, "E59.MirrorC", {"center": v(877.5, -625) * mm, "radius": 25 * mm});
            skCircle(sketch, "E60.MirrorC", {"center": v(877.5, -1125) * mm, "radius": 25 * mm});
            skCircle(sketch, "E61.MirrorC", {"center": v(877.5, -1375) * mm, "radius": 25 * mm});
            skCircle(sketch, "E62.MirrorC", {"center": v(877.5, -875) * mm, "radius": 25 * mm});
            skSolve(sketch);
        }
        {
            var Q0;
            Q0 = qSketchRegion(id + "F30", true);
            extrude(context, id + "F31", {"entities" : qUnion([Q0]), "operationType" : NewBodyOperationType.ADD, "depth" : 100 * mm, "offsetDistance" : 25 * mm, "hasSecondDirection" : true, "secondDirectionOppositeDirection" : true, "secondDirectionDepth" : 200 * mm});
        }
        {
            var Q0;
            Q0=makeQuery(id+"F31.opExtrude","CAP_EDGE",EDGE,{"disambiguationData":[OSD([sQuery(id+"F30.wireOp",EDGE,"E56.0.5.0")])],"isStart":true});
            var Q1;
            Q1=makeQuery(id+"F31.opExtrude","CAP_EDGE",EDGE,{"disambiguationData":[OSD([sQuery(id+"F30.wireOp",EDGE,"E56.0.4.0")])],"isStart":true});
            var Q2;
            Q2=makeQuery(id+"F31.opExtrude","CAP_EDGE",EDGE,{"disambiguationData":[OSD([sQuery(id+"F30.wireOp",EDGE,"E56.0.3.0")])],"isStart":true});
            var Q3;
            Q3=makeQuery(id+"F31.opExtrude","CAP_EDGE",EDGE,{"disambiguationData":[OSD([sQuery(id+"F30.wireOp",EDGE,"E56.0.2.0")])],"isStart":true});
            var Q4;
            Q4=makeQuery(id+"F31.opExtrude","CAP_EDGE",EDGE,{"disambiguationData":[OSD([sQuery(id+"F30.wireOp",EDGE,"E56.0.1.0")])],"isStart":true});
            var Q5;
            Q5=makeQuery(id+"F31.opExtrude","CAP_EDGE",EDGE,{"disambiguationData":[OSD([sQuery(id+"F30.wireOp",EDGE,"E55")])],"isStart":true});
            var Q6;
            Q6=makeQuery(id+"F31.opExtrude","CAP_EDGE",EDGE,{"disambiguationData":[OSD([sQuery(id+"F30.wireOp",EDGE,"E61.MirrorC")])],"isStart":true});
            var Q7;
            Q7=makeQuery(id+"F31.opExtrude","CAP_EDGE",EDGE,{"disambiguationData":[OSD([sQuery(id+"F30.wireOp",EDGE,"E60.MirrorC")])],"isStart":true});
            var Q8;
            Q8=makeQuery(id+"F31.opExtrude","CAP_EDGE",EDGE,{"disambiguationData":[OSD([sQuery(id+"F30.wireOp",EDGE,"E62.MirrorC")])],"isStart":true});
            var Q9;
            Q9=makeQuery(id+"F31.opExtrude","CAP_EDGE",EDGE,{"disambiguationData":[OSD([sQuery(id+"F30.wireOp",EDGE,"E59.MirrorC")])],"isStart":true});
            var Q10;
            Q10=makeQuery(id+"F31.opExtrude","CAP_EDGE",EDGE,{"disambiguationData":[OSD([sQuery(id+"F30.wireOp",EDGE,"E57.MirrorC")])],"isStart":true});
            var Q11;
            Q11=makeQuery(id+"F31.opExtrude","CAP_EDGE",EDGE,{"disambiguationData":[OSD([sQuery(id+"F30.wireOp",EDGE,"E58.MirrorC")])],"isStart":true});
            chamfer(context, id + "F32", {"entities" : qUnion([Q0, Q1, Q2, Q3, Q4, Q5, Q6, Q7, Q8, Q9, Q10, Q11]), "width" : 20 * mm, "tangentPropagation" : true});
        }
        {
            var Q0;
            Q0=makeQuery(id+"F1.opExtrude","SWEPT_FACE",FACE,{"disambiguationData":[OSD([sQuery(id+"F0.wireOp",EDGE,"E4"),sQuery(id+"F0.wireOp",EDGE,"E6.MirrorCS")])]});
            var sketch = newSketch(context, id + "F33", { "sketchPlane" : qUnion([Q0])});
            skLineSegment(sketch, "E63.bottom", {"start": v(-500, 0) * mm, "end": v(-450, 0) * mm});
            skLineSegment(sketch, "E63.top", {"start": v(-500, -50) * mm, "end": v(-450, -50) * mm});
            skLineSegment(sketch, "E63.left", {"start": v(-500, 0) * mm, "end": v(-500, -50) * mm});
            skLineSegment(sketch, "E63.right", {"start": v(-450, 0) * mm, "end": v(-450, -50) * mm});
            skLineSegment(sketch, "E64.bottom", {"start": v(500, 0) * mm, "end": v(450, 0) * mm});
            skLineSegment(sketch, "E64.top", {"start": v(500, -50) * mm, "end": v(450, -50) * mm});
            skLineSegment(sketch, "E64.left", {"start": v(500, 0) * mm, "end": v(500, -50) * mm});
            skLineSegment(sketch, "E64.right", {"start": v(450, 0) * mm, "end": v(450, -50) * mm});
            skLineSegment(sketch, "E65.bottom", {"start": v(-500, -1500) * mm, "end": v(-450, -1500) * mm});
            skLineSegment(sketch, "E65.top", {"start": v(-500, -1450) * mm, "end": v(-450, -1450) * mm});
            skLineSegment(sketch, "E65.left", {"start": v(-500, -1500) * mm, "end": v(-500, -1450) * mm});
            skLineSegment(sketch, "E65.right", {"start": v(-450, -1500) * mm, "end": v(-450, -1450) * mm});
            skLineSegment(sketch, "E66.bottom", {"start": v(500, -1500) * mm, "end": v(450, -1500) * mm});
            skLineSegment(sketch, "E66.top", {"start": v(500, -1450) * mm, "end": v(450, -1450) * mm});
            skLineSegment(sketch, "E66.left", {"start": v(500, -1500) * mm, "end": v(500, -1450) * mm});
            skLineSegment(sketch, "E66.right", {"start": v(450, -1500) * mm, "end": v(450, -1450) * mm});
            skSolve(sketch);
        }
        {
            var Q0;
            Q0 = qSketchRegion(id + "F33", true);
            extrude(context, id + "F34", {"entities" : qUnion([Q0]), "operationType" : NewBodyOperationType.ADD, "depth" : 500 * mm, "offsetDistance" : 25 * mm});
        }
        {
            var Q0;
            Q0=makeQuery(id+"F34.opExtrude","CAP_FACE",FACE,{"disambiguationData":[OSD([sQuery(id+"F33.wireOp",EDGE,"E65.bottom"),sQuery(id+"F33.wireOp",EDGE,"E65.top"),sQuery(id+"F33.wireOp",EDGE,"E65.left"),sQuery(id+"F33.wireOp",EDGE,"E65.right")])],"isStart":false});
            var sketch = newSketch(context, id + "F35", { "sketchPlane" : qUnion([Q0])});
            skLineSegment(sketch, "E67.bottom", {"start": v(-500, -1500) * mm, "end": v(500, -1500) * mm});
            skLineSegment(sketch, "E67.top", {"start": v(-500, 0) * mm, "end": v(500, 0) * mm});
            skLineSegment(sketch, "E67.left", {"start": v(-500, -1500) * mm, "end": v(-500, 0) * mm});
            skLineSegment(sketch, "E67.right", {"start": v(500, -1500) * mm, "end": v(500, 0) * mm});
            skSolve(sketch);
        }
        {
            var Q0;
            Q0 = qSketchRegion(id + "F35", true);
            extrude(context, id + "F36", {"entities" : qUnion([Q0]), "operationType" : NewBodyOperationType.ADD, "depth" : 25 * mm, "offsetDistance" : 25 * mm});
        }
    });
